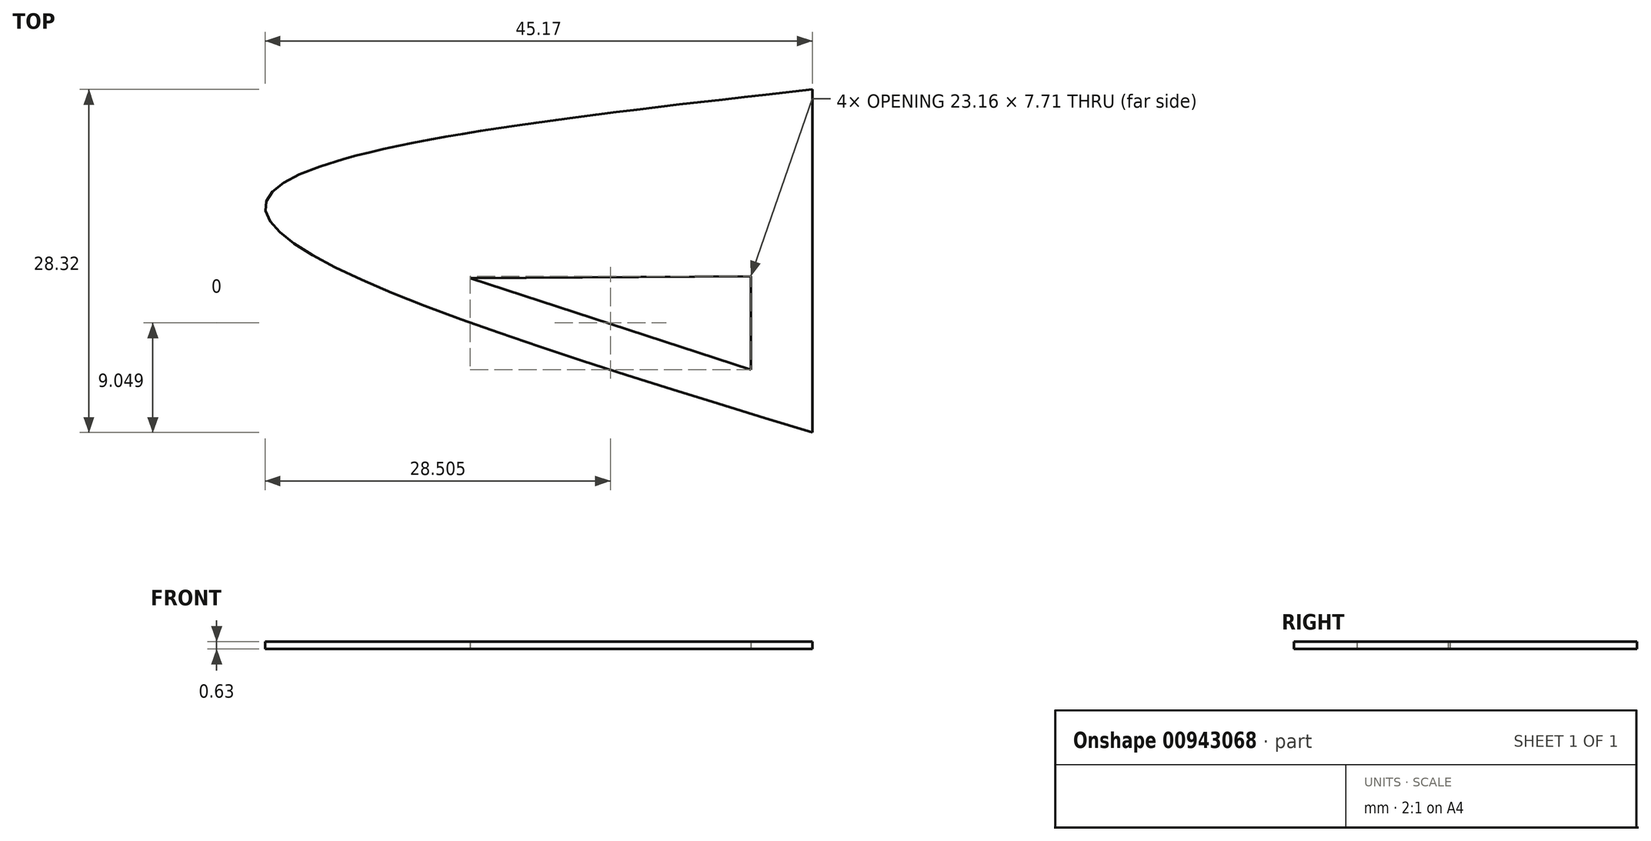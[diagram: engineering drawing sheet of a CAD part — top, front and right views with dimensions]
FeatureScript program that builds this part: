
annotation { "Feature Type Name" : "Feature", "Feature Type Description" : "" }
export const myFeature = defineFeature(function(context is Context, id is Id, definition is map)
    precondition{}
    {
        {
            var Q0;
            Q0=qCreatedBy(makeId("Top.planeOp"),FACE);
            var sketch = newSketch(context, id + "F0", { "sketchPlane" : qUnion([Q0])});
            skLineSegment(sketch, "E0", {"start": v(0, -18.72) * mm, "end": v(0, 9.6) * mm});
            skFitSpline(sketch, "E1", {"points": [v(0, -18.72) * mm, v(-45.16, 0) * mm, v(0, 9.6) * mm], "startDerivative": vector(-134.88, 41.34) * mm, "endDerivative": vector(136.17, 15.19) * mm});
            skLineSegment(sketch, "E2", {"start": v(-38.67, 3.87) * mm, "end": v(-38.67, -2.62) * mm});
            skLineSegment(sketch, "E3", {"start": v(-38.67, -2.62) * mm, "end": v(-3.82, -2.62) * mm});
            skPoint(sketch, "E3.endSnap0", {"position": v(0, -4.56) * mm});
            skLineSegment(sketch, "E4", {"start": v(0, -2.62) * mm, "end": v(0, 9.6) * mm});
            skLineSegment(sketch, "E5", {"start": v(-3.82, 9.18) * mm, "end": v(-3.82, -2.62) * mm});
            skLineSegment(sketch, "E6", {"start": v(-28.24, -6) * mm, "end": v(-5.09, -13.53) * mm});
            skLineSegment(sketch, "E7", {"start": v(-5.09, -13.53) * mm, "end": v(-5.09, -5.82) * mm});
            skLineSegment(sketch, "E8", {"start": v(-5.09, -5.82) * mm, "end": v(-28.24, -6) * mm});
            skSolve(sketch);
        }
        {
            var Q0;
            Q0 = qSketchRegion(id + "F0", true);
            extrude(context, id + "F1", {"entities" : qUnion([Q0]), "depth" : 0.63 * mm, "offsetDistance" : 25.4 * mm});
        }
    });
